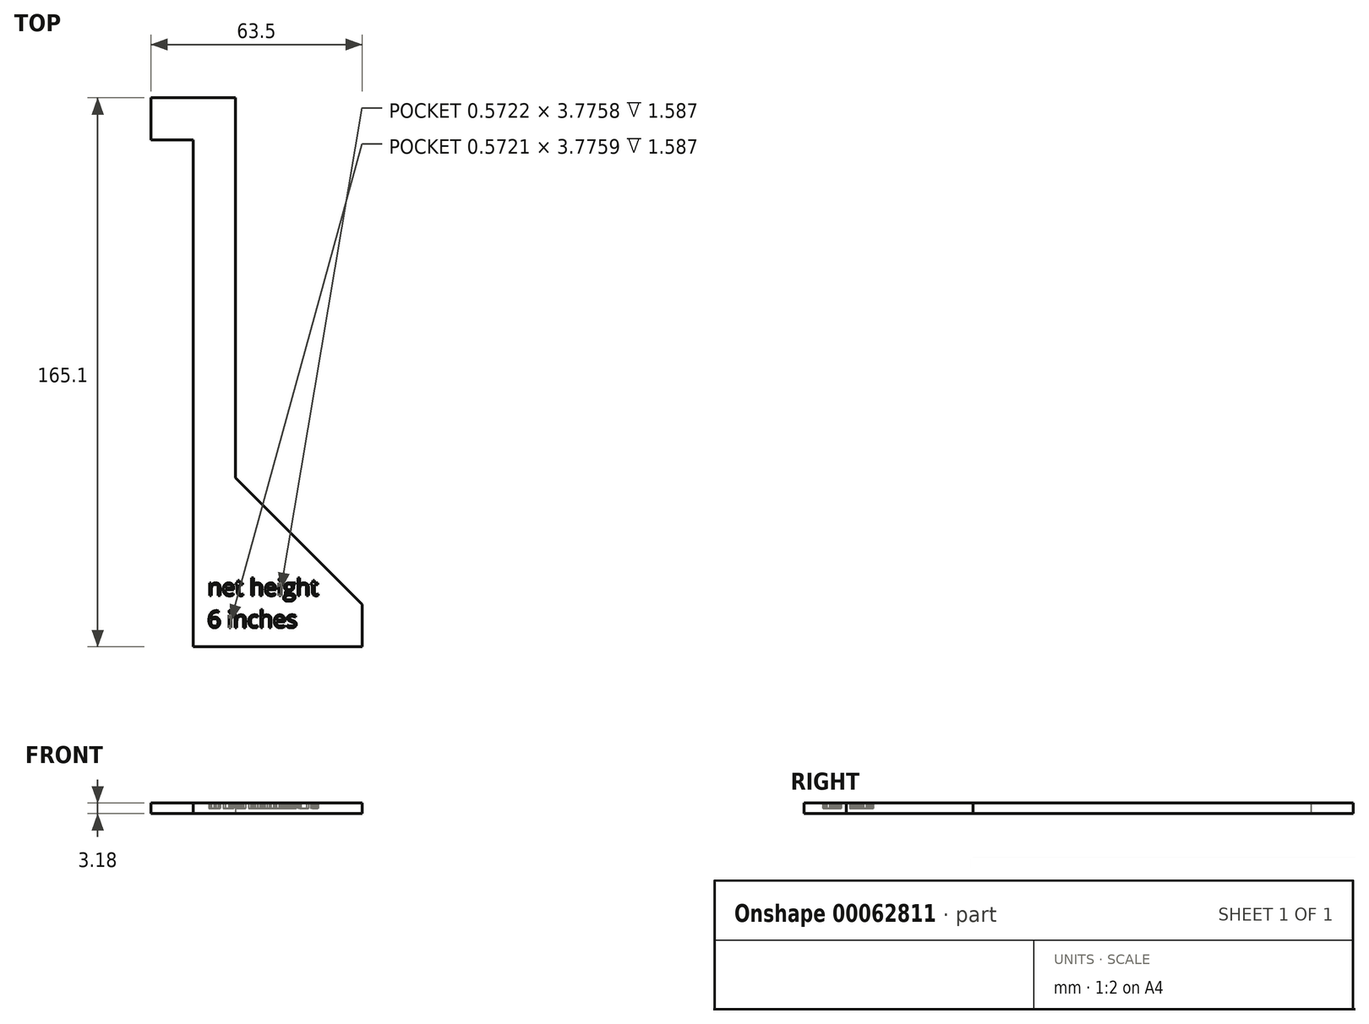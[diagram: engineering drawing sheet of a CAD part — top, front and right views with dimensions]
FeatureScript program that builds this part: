
annotation { "Feature Type Name" : "Feature", "Feature Type Description" : "" }
export const myFeature = defineFeature(function(context is Context, id is Id, definition is map)
    precondition{}
    {
        {
            var Q0;
            Q0=qCreatedBy(makeId("Top.planeOp"),FACE);
            var sketch = newSketch(context, id + "F0", { "sketchPlane" : qUnion([Q0])});
            skLineSegment(sketch, "E0", {"start": v(0, 0) * mm, "end": v(50.8, 0) * mm});
            skLineSegment(sketch, "E1", {"start": v(50.8, 0) * mm, "end": v(50.8, 12.7) * mm});
            skLineSegment(sketch, "E2", {"start": v(12.7, 50.8) * mm, "end": v(12.7, 165.1) * mm});
            skLineSegment(sketch, "E3", {"start": v(12.7, 165.1) * mm, "end": v(-12.7, 165.1) * mm});
            skLineSegment(sketch, "E4", {"start": v(-12.7, 165.1) * mm, "end": v(-12.7, 152.4) * mm});
            skLineSegment(sketch, "E5", {"start": v(-12.7, 152.4) * mm, "end": v(0, 152.4) * mm});
            skLineSegment(sketch, "E6", {"start": v(0, 152.4) * mm, "end": v(0, 0) * mm});
            skLineSegment(sketch, "E7", {"start": v(50.8, 12.7) * mm, "end": v(12.7, 50.8) * mm});
            skText(sketch, "E8", { "text": "net height\n6 inches", "fontName": "OpenSans-Regular.ttf"});
            const initialGuessF0  = {"E8": [0.0043, 0.01538, 1, 0, 0.00508]};
            skSetInitialGuess(sketch, initialGuessF0);
            skSolve(sketch);
        }
        {
            var Q0;
            Q0 = qSketchRegion(id + "F0", true);
            var Q1;
            Q1=makeQuery(id+"F0.imprint","IMPRINT",FACE,{"disambiguationData":[TD([[makeQuery(id+"F0.imprint","IMPRINT",EDGE,{"derivedFrom":sQuery(id+"F0.wireOp",EDGE,"E8.sketch_text.stroke-31")}),1.0]])]});
            var Q2;
            Q2=makeQuery(id+"F0.imprint","IMPRINT",FACE,{"disambiguationData":[TD([[makeQuery(id+"F0.imprint","IMPRINT",EDGE,{"derivedFrom":sQuery(id+"F0.wireOp",EDGE,"E8.sketch_text.stroke-200")}),1.0]])]});
            var Q3;
            Q3=makeQuery(id+"F0.imprint","IMPRINT",FACE,{"disambiguationData":[TD([[makeQuery(id+"F0.imprint","IMPRINT",EDGE,{"derivedFrom":sQuery(id+"F0.wireOp",EDGE,"E8.sketch_text.stroke-87")}),1.0]])]});
            var Q4;
            Q4=makeQuery(id+"F0.imprint","IMPRINT",FACE,{"disambiguationData":[TD([[makeQuery(id+"F0.imprint","IMPRINT",EDGE,{"derivedFrom":sQuery(id+"F0.wireOp",EDGE,"E8.sketch_text.stroke-142")}),1.0]])]});
            var Q5;
            Q5=makeQuery(id+"F0.imprint","IMPRINT",FACE,{"disambiguationData":[TD([[makeQuery(id+"F0.imprint","IMPRINT",EDGE,{"derivedFrom":sQuery(id+"F0.wireOp",EDGE,"E8.sketch_text.stroke-133")}),1.0]])]});
            var Q6;
            Q6=makeQuery(id+"F0.imprint","IMPRINT",FACE,{"disambiguationData":[TD([[makeQuery(id+"F0.imprint","IMPRINT",EDGE,{"derivedFrom":sQuery(id+"F0.wireOp",EDGE,"E8.sketch_text.stroke-286")}),1.0]])]});
            extrude(context, id + "F1", {"entities" : qUnion([Q0, Q1, Q2, Q3, Q4, Q5, Q6]), "depth" : 3.17 * mm});
        }
        {
            var Q0;
            Q0=makeQuery(id+"F0.imprint","IMPRINT",FACE,{"disambiguationData":[TD([[makeQuery(id+"F0.imprint","IMPRINT",EDGE,{"derivedFrom":sQuery(id+"F0.wireOp",EDGE,"E8.sketch_text.stroke-96")}),-1.0]])]});
            var Q1;
            Q1=makeQuery(id+"F0.imprint","IMPRINT",FACE,{"disambiguationData":[TD([[makeQuery(id+"F0.imprint","IMPRINT",EDGE,{"derivedFrom":sQuery(id+"F0.wireOp",EDGE,"E8.sketch_text.stroke-92")}),-1.0]])]});
            var Q2;
            Q2=makeQuery(id+"F0.imprint","IMPRINT",FACE,{"disambiguationData":[TD([[makeQuery(id+"F0.imprint","IMPRINT",EDGE,{"derivedFrom":sQuery(id+"F0.wireOp",EDGE,"E8.sketch_text.stroke-73")}),-1.0]])]});
            var Q3;
            Q3=makeQuery(id+"F0.imprint","IMPRINT",FACE,{"disambiguationData":[TD([[makeQuery(id+"F0.imprint","IMPRINT",EDGE,{"derivedFrom":sQuery(id+"F0.wireOp",EDGE,"E8.sketch_text.stroke-55")}),-1.0]])]});
            var Q4;
            Q4=makeQuery(id+"F0.imprint","IMPRINT",FACE,{"disambiguationData":[TD([[makeQuery(id+"F0.imprint","IMPRINT",EDGE,{"derivedFrom":sQuery(id+"F0.wireOp",EDGE,"E8.sketch_text.stroke-36")}),-1.0]])]});
            var Q5;
            Q5=makeQuery(id+"F0.imprint","IMPRINT",FACE,{"disambiguationData":[TD([[makeQuery(id+"F0.imprint","IMPRINT",EDGE,{"derivedFrom":sQuery(id+"F0.wireOp",EDGE,"E8.sketch_text.stroke-17")}),-1.0]])]});
            var Q6;
            Q6=makeQuery(id+"F0.imprint","IMPRINT",FACE,{"disambiguationData":[TD([[makeQuery(id+"F0.imprint","IMPRINT",EDGE,{"derivedFrom":sQuery(id+"F0.wireOp",EDGE,"E8.sketch_text.stroke-0")}),-1.0]])]});
            var Q7;
            Q7=makeQuery(id+"F0.imprint","IMPRINT",FACE,{"disambiguationData":[TD([[makeQuery(id+"F0.imprint","IMPRINT",EDGE,{"derivedFrom":sQuery(id+"F0.wireOp",EDGE,"E8.sketch_text.stroke-104")}),-1.0]])]});
            var Q8;
            Q8=makeQuery(id+"F0.imprint","IMPRINT",FACE,{"disambiguationData":[TD([[makeQuery(id+"F0.imprint","IMPRINT",EDGE,{"derivedFrom":sQuery(id+"F0.wireOp",EDGE,"E8.sketch_text.stroke-148")}),-1.0]])]});
            var Q9;
            Q9=makeQuery(id+"F0.imprint","IMPRINT",FACE,{"disambiguationData":[TD([[makeQuery(id+"F0.imprint","IMPRINT",EDGE,{"derivedFrom":sQuery(id+"F0.wireOp",EDGE,"E8.sketch_text.stroke-166")}),-1.0]])]});
            var Q10;
            Q10=makeQuery(id+"F0.imprint","IMPRINT",FACE,{"disambiguationData":[TD([[makeQuery(id+"F0.imprint","IMPRINT",EDGE,{"derivedFrom":sQuery(id+"F0.wireOp",EDGE,"E8.sketch_text.stroke-185")}),-1.0]])]});
            var Q11;
            Q11=makeQuery(id+"F0.imprint","IMPRINT",FACE,{"disambiguationData":[TD([[makeQuery(id+"F0.imprint","IMPRINT",EDGE,{"derivedFrom":sQuery(id+"F0.wireOp",EDGE,"E8.sketch_text.stroke-210")}),-1.0]])]});
            var Q12;
            Q12=makeQuery(id+"F0.imprint","IMPRINT",FACE,{"disambiguationData":[TD([[makeQuery(id+"F0.imprint","IMPRINT",EDGE,{"derivedFrom":sQuery(id+"F0.wireOp",EDGE,"E8.sketch_text.stroke-214")}),-1.0]])]});
            var Q13;
            Q13=makeQuery(id+"F0.imprint","IMPRINT",FACE,{"disambiguationData":[TD([[makeQuery(id+"F0.imprint","IMPRINT",EDGE,{"derivedFrom":sQuery(id+"F0.wireOp",EDGE,"E8.sketch_text.stroke-222")}),-1.0]])]});
            var Q14;
            Q14=makeQuery(id+"F0.imprint","IMPRINT",FACE,{"disambiguationData":[TD([[makeQuery(id+"F0.imprint","IMPRINT",EDGE,{"derivedFrom":sQuery(id+"F0.wireOp",EDGE,"E8.sketch_text.stroke-239")}),-1.0]])]});
            var Q15;
            Q15=makeQuery(id+"F0.imprint","IMPRINT",FACE,{"disambiguationData":[TD([[makeQuery(id+"F0.imprint","IMPRINT",EDGE,{"derivedFrom":sQuery(id+"F0.wireOp",EDGE,"E8.sketch_text.stroke-254")}),-1.0]])]});
            var Q16;
            Q16=makeQuery(id+"F0.imprint","IMPRINT",FACE,{"disambiguationData":[TD([[makeQuery(id+"F0.imprint","IMPRINT",EDGE,{"derivedFrom":sQuery(id+"F0.wireOp",EDGE,"E8.sketch_text.stroke-291")}),-1.0]])]});
            var Q17;
            Q17=makeQuery(id+"F0.imprint","IMPRINT",FACE,{"disambiguationData":[TD([[makeQuery(id+"F0.imprint","IMPRINT",EDGE,{"derivedFrom":sQuery(id+"F0.wireOp",EDGE,"E8.sketch_text.stroke-272")}),-1.0]])]});
            extrude(context, id + "F2", {"entities" : qUnion([Q0, Q1, Q2, Q3, Q4, Q5, Q6, Q7, Q8, Q9, Q10, Q11, Q12, Q13, Q14, Q15, Q16, Q17]), "operationType" : NewBodyOperationType.ADD, "depth" : 1.59 * mm});
        }
    });
